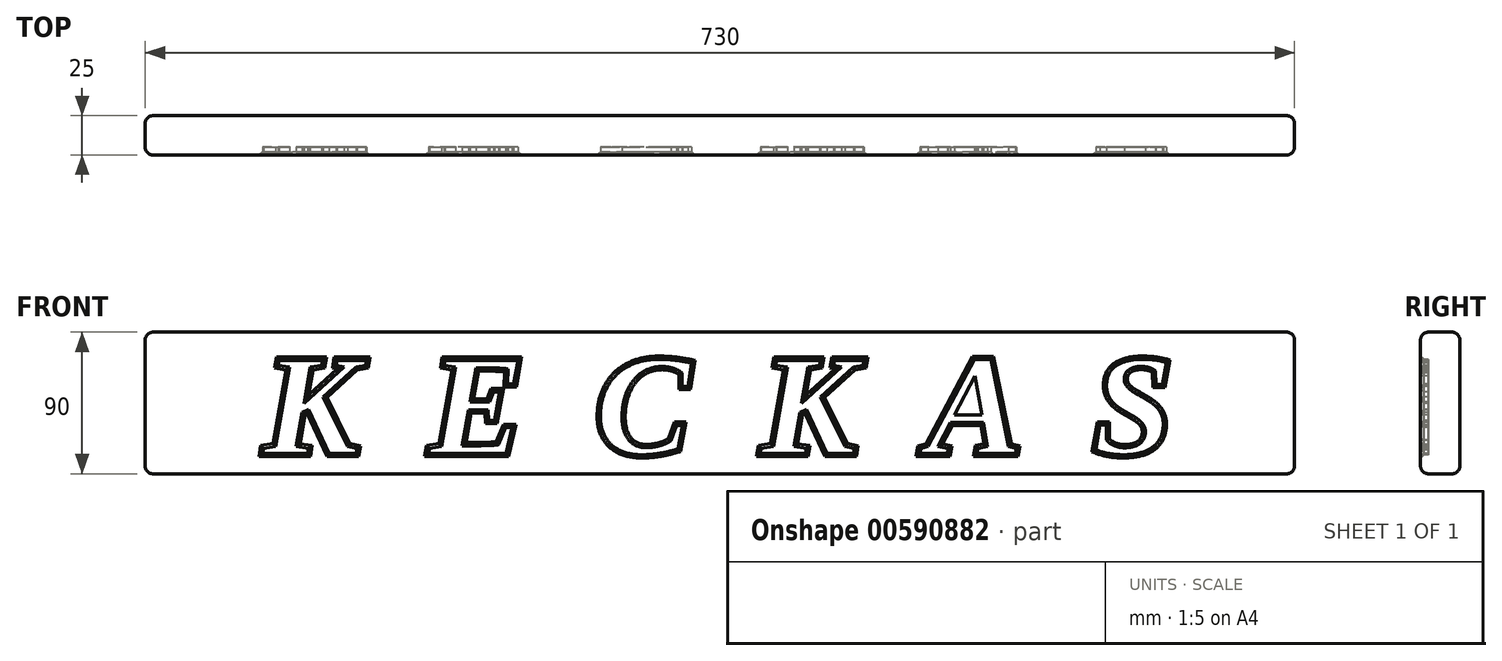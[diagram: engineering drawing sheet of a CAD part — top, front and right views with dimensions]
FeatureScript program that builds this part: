
annotation { "Feature Type Name" : "Feature", "Feature Type Description" : "" }
export const myFeature = defineFeature(function(context is Context, id is Id, definition is map)
    precondition{}
    {
        {
            var Q0;
            Q0=qCreatedBy(makeId("Front.planeOp"),FACE);
            var sketch = newSketch(context, id + "F0", { "sketchPlane" : qUnion([Q0])});
            skLineSegment(sketch, "E0.bottom", {"start": v(5, 0) * mm, "end": v(725, 0) * mm});
            skLineSegment(sketch, "E0.top", {"start": v(5, 90) * mm, "end": v(725, 90) * mm});
            skLineSegment(sketch, "E0.left", {"start": v(0, 5) * mm, "end": v(0, 85) * mm});
            skLineSegment(sketch, "E0.right", {"start": v(730, 5) * mm, "end": v(730, 85) * mm});
            skPoint(sketch, "E1.visualSharp", {"position": v(0, 90) * mm});
            skArc(sketch, "E1.filletArc", {"start": v(5, 90) * mm, "mid": v(1.46, 88.54) * mm, "end": v(0, 85) * mm});
            skPoint(sketch, "E2.visualSharp", {"position": v(730, 90) * mm});
            skArc(sketch, "E2.filletArc", {"start": v(730, 85) * mm, "mid": v(728.54, 88.54) * mm, "end": v(725, 90) * mm});
            skPoint(sketch, "E3.visualSharp", {"position": v(730, 0) * mm});
            skArc(sketch, "E3.filletArc", {"start": v(725, 0) * mm, "mid": v(728.54, 1.46) * mm, "end": v(730, 5) * mm});
            skPoint(sketch, "E4.visualSharp", {"position": v(0, 0) * mm});
            skArc(sketch, "E4.filletArc", {"start": v(0, 5) * mm, "mid": v(1.46, 1.46) * mm, "end": v(5, 0) * mm});
            skSolve(sketch);
        }
        {
            var Q0;
            Q0 = qSketchRegion(id + "F0", true);
            extrude(context, id + "F1", {"entities" : qUnion([Q0]), "depth" : 25 * mm, "offsetDistance" : 25 * mm});
        }
        {
            var Q0;
            Q0=makeQuery(id+"F1.opExtrude","CAP_EDGE",EDGE,{"disambiguationData":[OSD([sQuery(id+"F0.wireOp",EDGE,"E0.bottom")])],"isStart":false});
            var Q1;
            Q1=makeQuery(id+"F1.opExtrude","CAP_EDGE",EDGE,{"disambiguationData":[OSD([sQuery(id+"F0.wireOp",EDGE,"E0.top")])],"isStart":true});
            fillet(context, id + "F2", {"entities" : qUnion([Q0, Q1]), "radius" : 5 * mm, "tangentPropagation" : true, "allowEdgeOverflow" : false});
        }
        {
            var Q0;
            Q0=makeQuery(id+"F1.opExtrude","CAP_FACE",FACE,{"disambiguationData":[OSD([sQuery(id+"F0.wireOp",EDGE,"E0.bottom"),sQuery(id+"F0.wireOp",EDGE,"E0.top"),sQuery(id+"F0.wireOp",EDGE,"E0.left"),sQuery(id+"F0.wireOp",EDGE,"E0.right"),sQuery(id+"F0.wireOp",EDGE,"E1.filletArc"),sQuery(id+"F0.wireOp",EDGE,"E2.filletArc"),sQuery(id+"F0.wireOp",EDGE,"E3.filletArc"),sQuery(id+"F0.wireOp",EDGE,"E4.filletArc")])],"isStart":false});
            var sketch = newSketch(context, id + "F3", { "sketchPlane" : qUnion([Q0])});
            skLineSegment(sketch, "E5", {"start": v(130, 289.6) * mm, "end": v(130, -289.19) * mm, "construction": true});
            skLineSegment(sketch, "E6", {"start": v(365, -285.2) * mm, "end": v(365, 315.03) * mm, "construction": true});
            skPoint(sketch, "E6.startSnap0", {"position": v(365, 5) * mm});
            skLineSegment(sketch, "E7.MirrorCS", {"start": v(600, 289.6) * mm, "end": v(600, -289.19) * mm, "construction": true});
            skText(sketch, "E8", { "text": "K  E  C  K  A  S", "fontName": "Tinos-BoldItalic.ttf"});
            const initialGuessF3  = {"E8": [0.07524, 0.013, 1, 0, 0.065]};
            skSetInitialGuess(sketch, initialGuessF3);
            skSolve(sketch);
        }
        {
            var Q0;
            Q0 = qSketchRegion(id + "F3", true);
            extrude(context, id + "F4", {"entities" : qUnion([Q0]), "operationType" : NewBodyOperationType.REMOVE, "oppositeDirection" : true, "depth" : 5 * mm, "offsetDistance" : 25 * mm});
        }
        {
            var Q0;
            {var subQ0=sQuery(id+"F0.wireOp",EDGE,"E0.left");var subQ1=sQuery(id+"F0.wireOp",EDGE,"E0.top");var subQ2=sQuery(id+"F0.wireOp",EDGE,"E0.bottom");var subQ3=sQuery(id+"F0.wireOp",EDGE,"E1.filletArc");var subQ4=sQuery(id+"F0.wireOp",EDGE,"E2.filletArc");var subQ5=sQuery(id+"F0.wireOp",EDGE,"E3.filletArc");var subQ6=sQuery(id+"F0.wireOp",EDGE,"E4.filletArc");var subQ7=sQuery(id+"F0.wireOp",EDGE,"E0.right");Q0=makeQuery(id+"F4.boolean.opBoolean","SPLIT",FACE,{"disambiguationData":[TD([makeQuery(id+"F4.opExtrude","SWEPT_FACE",FACE,{"disambiguationData":[OSD([sQuery(id+"F3.wireOp",EDGE,"E8.sketch_text.stroke-0")])]})])],"derivedFrom":makeQuery(id+"F1.opExtrude","CAP_FACE",FACE,{"disambiguationData":[OSD([subQ2,subQ1,subQ0,subQ7,subQ3,subQ4,subQ5,subQ6])],"isStart":false})});}
            chamfer(context, id + "F5", {"entities" : qUnion([Q0]), "width" : 2 * mm, "tangentPropagation" : true});
        }
    });
